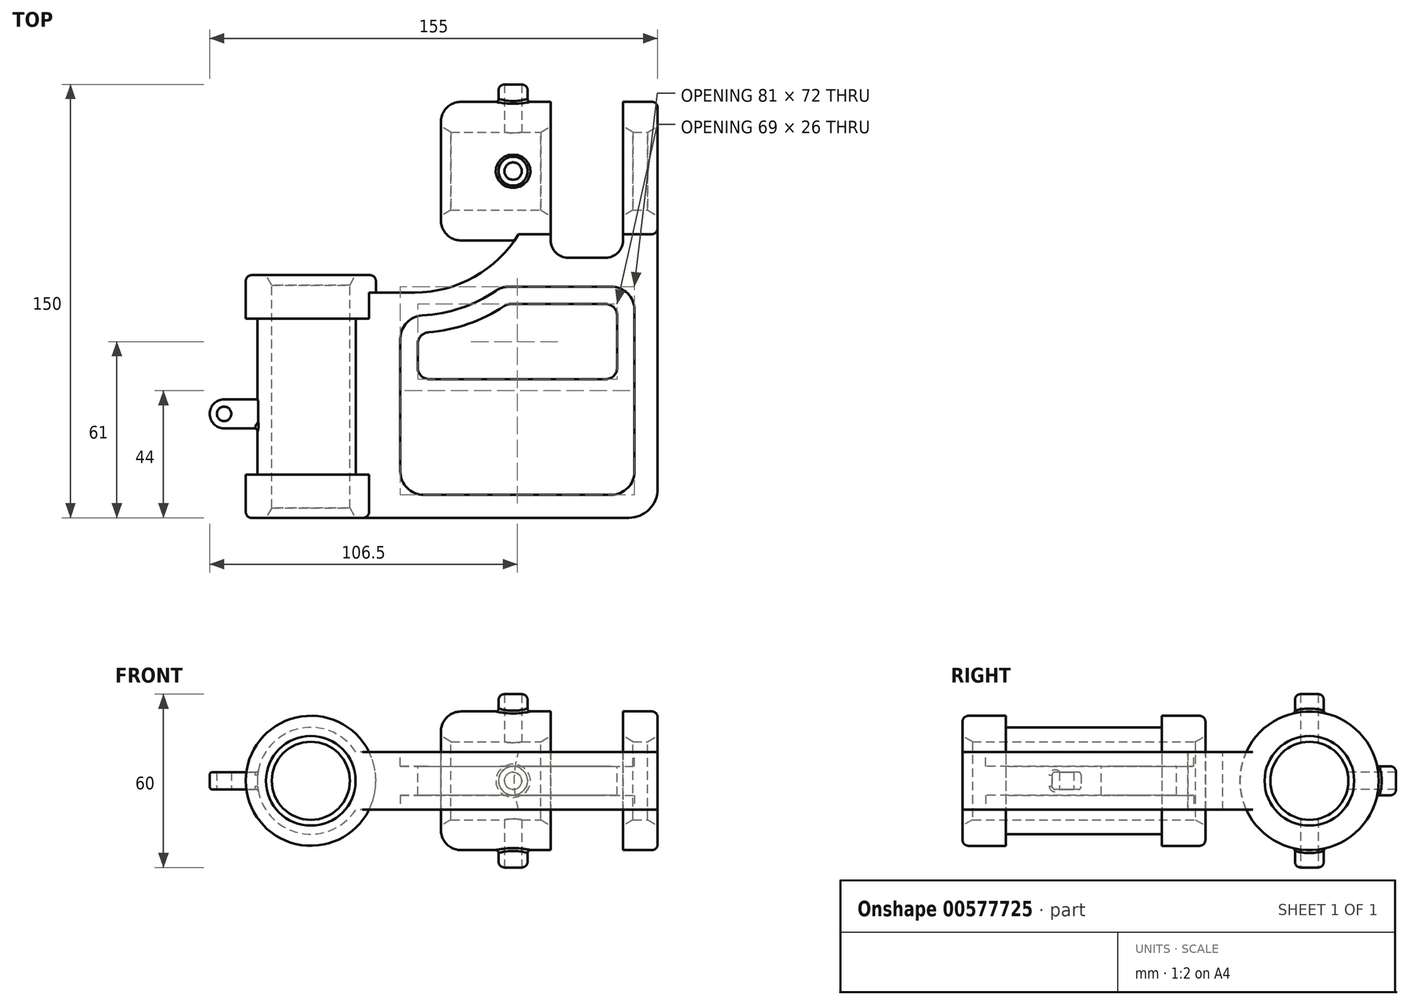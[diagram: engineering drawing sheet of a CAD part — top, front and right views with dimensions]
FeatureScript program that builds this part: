
annotation { "Feature Type Name" : "Feature", "Feature Type Description" : "" }
export const myFeature = defineFeature(function(context is Context, id is Id, definition is map)
    precondition{}
    {
        {
            var Q0;
            Q0=qCreatedBy(makeId("Top.planeOp"),FACE);
            var sketch = newSketch(context, id + "F0", { "sketchPlane" : qUnion([Q0])});
            skLineSegment(sketch, "E0.bottom", {"start": v(-10, 0) * mm, "end": v(-120, 0) * mm});
            skLineSegment(sketch, "E0.top", {"start": v(0, 120) * mm, "end": v(-42, 120) * mm});
            skLineSegment(sketch, "E0.left", {"start": v(0, 10) * mm, "end": v(0, 120) * mm});
            skLineSegment(sketch, "E0.right", {"start": v(-120, 0) * mm, "end": v(-120, 78) * mm});
            skArc(sketch, "E1", {"start": v(-84, 78) * mm, "mid": v(-54.3, 90.3) * mm, "end": v(-42, 120) * mm});
            skLineSegment(sketch, "E2", {"start": v(-84, 78) * mm, "end": v(-120, 78) * mm});
            skPoint(sketch, "E3.visualSharp", {"position": v(0, 0) * mm});
            skArc(sketch, "E3.filletArc", {"start": v(-10, 0) * mm, "mid": v(-2.93, 2.93) * mm, "end": v(0, 10) * mm});
            skSolve(sketch);
        }
        {
            var Q0;
            Q0 = qSketchRegion(id + "F0", true);
            extrude(context, id + "F1", {"entities" : qUnion([Q0]), "endBound" : BoundingType.SYMMETRIC, "depth" : 20 * mm, "offsetDistance" : 25 * mm});
        }
        {
            var Q0;
            Q0=qCreatedBy(makeId("Top.planeOp"),FACE);
            var sketch = newSketch(context, id + "F2", { "sketchPlane" : qUnion([Q0])});
            skLineSegment(sketch, "E4", {"start": v(-75, 120) * mm, "end": v(0, 120) * mm});
            skLineSegment(sketch, "E5", {"start": v(0, 120) * mm, "end": v(0, 142) * mm});
            skLineSegment(sketch, "E6", {"start": v(-2, 144) * mm, "end": v(-68, 144) * mm});
            skLineSegment(sketch, "E7", {"start": v(-75, 137) * mm, "end": v(-75, 120) * mm});
            skLineSegment(sketch, "E8", {"start": v(-75, 120) * mm, "end": v(-98.48, 120) * mm, "construction": true});
            skPoint(sketch, "E9.visualSharp", {"position": v(-75, 144) * mm});
            skArc(sketch, "E9.filletArc", {"start": v(-68, 144) * mm, "mid": v(-72.95, 141.95) * mm, "end": v(-75, 137) * mm});
            skPoint(sketch, "E10.visualSharp", {"position": v(0, 144) * mm});
            skArc(sketch, "E10.filletArc", {"start": v(0, 142) * mm, "mid": v(-0.59, 143.41) * mm, "end": v(-2, 144) * mm});
            skLineSegment(sketch, "E11", {"start": v(-75, 133.5) * mm, "end": v(0, 133.5) * mm, "construction": true});
            skSolve(sketch);
        }
        {
            var Q0;
            Q0=makeQuery(id+"F2.imprint","IMPRINT",FACE,{"disambiguationData":[TD([[makeQuery(id+"F2.imprint","IMPRINT",EDGE,{"derivedFrom":sQuery(id+"F2.wireOp",EDGE,"E4")}),1.0]])]});
            var Q1;
            Q1=sQuery(id+"F2.wireOp",EDGE,"E8");
            revolve(context, id + "F3", {"operationType" : NewBodyOperationType.ADD, "entities" : qUnion([Q0]), "axis" : qUnion([Q1]), "revolveType" : RevolveType.FULL});
        }
        {
            var Q0;
            Q0=qCreatedBy(makeId("Top.planeOp"),FACE);
            var sketch = newSketch(context, id + "F4", { "sketchPlane" : qUnion([Q0])});
            skLineSegment(sketch, "E12", {"start": v(-120, 0) * mm, "end": v(-120, 84) * mm});
            skLineSegment(sketch, "E13", {"start": v(-120, 84) * mm, "end": v(-140.5, 84) * mm});
            skLineSegment(sketch, "E14", {"start": v(-142.5, 82) * mm, "end": v(-142.5, 69) * mm});
            skLineSegment(sketch, "E15", {"start": v(-142.5, 69) * mm, "end": v(-138.5, 69) * mm});
            skLineSegment(sketch, "E16", {"start": v(-138.5, 69) * mm, "end": v(-138.5, 15) * mm});
            skLineSegment(sketch, "E17", {"start": v(-120, 42) * mm, "end": v(-294.47, 42) * mm, "construction": true});
            skLineSegment(sketch, "E18.MirrorCS", {"start": v(-142.5, 15) * mm, "end": v(-138.5, 15) * mm});
            skLineSegment(sketch, "E19.MirrorCS", {"start": v(-142.5, 2) * mm, "end": v(-142.5, 15) * mm});
            skLineSegment(sketch, "E20.MirrorCS", {"start": v(-120, 0) * mm, "end": v(-140.5, 0) * mm});
            skLineSegment(sketch, "E21", {"start": v(-120, 84) * mm, "end": v(-120, 176) * mm, "construction": true});
            skLineSegment(sketch, "E22", {"start": v(-133.5, 84) * mm, "end": v(-133.5, 0) * mm, "construction": true});
            skPoint(sketch, "E23.visualSharp", {"position": v(-142.5, 84) * mm});
            skArc(sketch, "E23.filletArc", {"start": v(-140.5, 84) * mm, "mid": v(-141.91, 83.41) * mm, "end": v(-142.5, 82) * mm});
            skPoint(sketch, "E24.visualSharp", {"position": v(-142.5, 0) * mm});
            skArc(sketch, "E24.filletArc", {"start": v(-142.5, 2) * mm, "mid": v(-141.91, 0.59) * mm, "end": v(-140.5, 0) * mm});
            skSolve(sketch);
        }
        {
            var Q0;
            Q0=makeQuery(id+"F4.imprint","IMPRINT",FACE,{"disambiguationData":[TD([[makeQuery(id+"F4.imprint","IMPRINT",EDGE,{"derivedFrom":sQuery(id+"F4.wireOp",EDGE,"E12")}),1.0]])]});
            var Q1;
            Q1 = qConstructionFilter(qBodyType(qCreatedBy(id + "F4" ,EDGE), BodyType.WIRE), ConstructionObject.NO);
            var Q2;
            Q2=sQuery(id+"F4.wireOp",EDGE,"E21");
            revolve(context, id + "F5", {"operationType" : NewBodyOperationType.ADD, "entities" : qUnion([Q0]), "surfaceEntities" : qUnion([Q1]), "axis" : qUnion([Q2]), "revolveType" : RevolveType.FULL});
        }
        {
            var Q0;
            Q0=qCreatedBy(makeId("Top.planeOp"),FACE);
            var sketch = newSketch(context, id + "F6", { "sketchPlane" : qUnion([Q0])});
            skLineSegment(sketch, "E25", {"start": v(-55, 120) * mm, "end": v(-55, 148) * mm});
            skLineSegment(sketch, "E26", {"start": v(-53, 150) * mm, "end": v(-50, 150) * mm});
            skLineSegment(sketch, "E27", {"start": v(-50, 150) * mm, "end": v(-50, 120) * mm});
            skLineSegment(sketch, "E28", {"start": v(-50, 120) * mm, "end": v(-55, 120) * mm});
            skLineSegment(sketch, "E29", {"start": v(-53, 120) * mm, "end": v(-53, 150) * mm, "construction": true});
            skPoint(sketch, "E30.visualSharp", {"position": v(-55, 150) * mm});
            skArc(sketch, "E30.filletArc", {"start": v(-53, 150) * mm, "mid": v(-54.41, 149.41) * mm, "end": v(-55, 148) * mm});
            skLineSegment(sketch, "E31", {"start": v(-50, 150) * mm, "end": v(-50, 202.5) * mm, "construction": true});
            skSolve(sketch);
        }
        {
            var Q0;
            Q0=makeQuery(id+"F6.imprint","IMPRINT",FACE,{"disambiguationData":[TD([[makeQuery(id+"F6.imprint","IMPRINT",EDGE,{"derivedFrom":sQuery(id+"F6.wireOp",EDGE,"E25")}),-1.0]])]});
            var Q1;
            Q1=sQuery(id+"F6.wireOp",EDGE,"E31");
            revolve(context, id + "F7", {"entities" : qUnion([Q0]), "axis" : qUnion([Q1]), "revolveType" : RevolveType.FULL});
        }
        {
            var Q0;
            Q0=qCreatedBy(makeId("Top.planeOp"),FACE);
            var sketch = newSketch(context, id + "F8", { "sketchPlane" : qUnion([Q0])});
            skLineSegment(sketch, "E32.bottom", {"start": v(-50, 150) * mm, "end": v(-53, 150) * mm});
            skLineSegment(sketch, "E32.top", {"start": v(-50, 120) * mm, "end": v(-53, 120) * mm});
            skLineSegment(sketch, "E32.left", {"start": v(-50, 150) * mm, "end": v(-50, 120) * mm});
            skLineSegment(sketch, "E32.right", {"start": v(-53, 150) * mm, "end": v(-53, 120) * mm});
            skLineSegment(sketch, "E33", {"start": v(-50, 150) * mm, "end": v(-50, 168.1) * mm, "construction": true});
            skSolve(sketch);
        }
        {
            var Q0;
            Q0 = qSketchRegion(id + "F8", true);
            var Q1;
            Q1=sQuery(id+"F8.wireOp",EDGE,"E33");
            revolve(context, id + "F9", {"entities" : qUnion([Q0]), "axis" : qUnion([Q1]), "revolveType" : RevolveType.FULL});
        }
        {
            var Q0;
            Q0=makeQuery(id+"F7.opRevolve","SWEPT_BODY",BODY,{"disambiguationData":[OSD([sQuery(id+"F6.wireOp",EDGE,"E25"),sQuery(id+"F6.wireOp",EDGE,"E26"),sQuery(id+"F6.wireOp",EDGE,"E27"),sQuery(id+"F6.wireOp",EDGE,"E28"),sQuery(id+"F6.wireOp",EDGE,"E30.filletArc")])]});
            var Q1;
            Q1=makeQuery(id+"F9.opRevolve","SWEPT_BODY",BODY,{"disambiguationData":[OSD([sQuery(id+"F8.wireOp",EDGE,"E32.bottom"),sQuery(id+"F8.wireOp",EDGE,"E32.top"),sQuery(id+"F8.wireOp",EDGE,"E32.left"),sQuery(id+"F8.wireOp",EDGE,"E32.right")])]});
            var Q2;
            Q2=sQuery(id+"F2.wireOp",EDGE,"E8");
            circularPattern(context, id + "F10", {"entities" : qUnion([Q0, Q1]), "axis" : qUnion([Q2]), "angle" : 90 * degree, "instanceCount" : 2, "oppositeDirection" : true, "equalSpace" : true});
        }
        {
            var Q0;
            Q0=makeQuery(id+"F7.opRevolve","SWEPT_BODY",BODY,{"disambiguationData":[OSD([sQuery(id+"F6.wireOp",EDGE,"E25"),sQuery(id+"F6.wireOp",EDGE,"E26"),sQuery(id+"F6.wireOp",EDGE,"E27"),sQuery(id+"F6.wireOp",EDGE,"E28"),sQuery(id+"F6.wireOp",EDGE,"E30.filletArc")])]});
            var Q1;
            Q1=makeQuery(id+"F9.opRevolve","SWEPT_BODY",BODY,{"disambiguationData":[OSD([sQuery(id+"F8.wireOp",EDGE,"E32.bottom"),sQuery(id+"F8.wireOp",EDGE,"E32.top"),sQuery(id+"F8.wireOp",EDGE,"E32.left"),sQuery(id+"F8.wireOp",EDGE,"E32.right")])]});
            var Q2;
            Q2=sQuery(id+"F2.wireOp",EDGE,"E8");
            circularPattern(context, id + "F11", {"entities" : qUnion([Q0, Q1]), "axis" : qUnion([Q2]), "angle" : 90 * degree, "instanceCount" : 2, "equalSpace" : true});
        }
        {
            var Q0;
            Q0=makeQuery(id+"F1.opExtrude","SWEPT_BODY",BODY,{"disambiguationData":[OSD([sQuery(id+"F0.wireOp",EDGE,"E0.bottom"),sQuery(id+"F0.wireOp",EDGE,"E0.top"),sQuery(id+"F0.wireOp",EDGE,"E0.left"),sQuery(id+"F0.wireOp",EDGE,"E0.right"),sQuery(id+"F0.wireOp",EDGE,"E1"),sQuery(id+"F0.wireOp",EDGE,"E2"),sQuery(id+"F0.wireOp",EDGE,"E3.filletArc")])]});
            var Q1;
            Q1=makeQuery(id+"F10.opPattern","COPY",BODY,{"derivedFrom":makeQuery(id+"F7.opRevolve","SWEPT_BODY",BODY,{"disambiguationData":[OSD([sQuery(id+"F6.wireOp",EDGE,"E25"),sQuery(id+"F6.wireOp",EDGE,"E26"),sQuery(id+"F6.wireOp",EDGE,"E27"),sQuery(id+"F6.wireOp",EDGE,"E28"),sQuery(id+"F6.wireOp",EDGE,"E30.filletArc")])]}),"instanceName":"1"});
            var Q2;
            Q2=makeQuery(id+"F7.opRevolve","SWEPT_BODY",BODY,{"disambiguationData":[OSD([sQuery(id+"F6.wireOp",EDGE,"E25"),sQuery(id+"F6.wireOp",EDGE,"E26"),sQuery(id+"F6.wireOp",EDGE,"E27"),sQuery(id+"F6.wireOp",EDGE,"E28"),sQuery(id+"F6.wireOp",EDGE,"E30.filletArc")])]});
            var Q3;
            Q3=makeQuery(id+"F11.opPattern","COPY",BODY,{"derivedFrom":makeQuery(id+"F7.opRevolve","SWEPT_BODY",BODY,{"disambiguationData":[OSD([sQuery(id+"F6.wireOp",EDGE,"E25"),sQuery(id+"F6.wireOp",EDGE,"E26"),sQuery(id+"F6.wireOp",EDGE,"E27"),sQuery(id+"F6.wireOp",EDGE,"E28"),sQuery(id+"F6.wireOp",EDGE,"E30.filletArc")])]}),"instanceName":"1"});
            booleanBodies(context, id + "F12", {"operationType" : BooleanOperationType.UNION, "tools" : qUnion([Q0, Q1, Q2, Q3])});
        }
        {
            var Q0;
            Q0=makeQuery(id+"F9.opRevolve","SWEPT_BODY",BODY,{"disambiguationData":[OSD([sQuery(id+"F8.wireOp",EDGE,"E32.bottom"),sQuery(id+"F8.wireOp",EDGE,"E32.top"),sQuery(id+"F8.wireOp",EDGE,"E32.left"),sQuery(id+"F8.wireOp",EDGE,"E32.right")])]});
            var Q1;
            Q1=makeQuery(id+"F10.opPattern","COPY",BODY,{"derivedFrom":makeQuery(id+"F9.opRevolve","SWEPT_BODY",BODY,{"disambiguationData":[OSD([sQuery(id+"F8.wireOp",EDGE,"E32.bottom"),sQuery(id+"F8.wireOp",EDGE,"E32.top"),sQuery(id+"F8.wireOp",EDGE,"E32.left"),sQuery(id+"F8.wireOp",EDGE,"E32.right")])]}),"instanceName":"1"});
            var Q2;
            Q2=makeQuery(id+"F11.opPattern","COPY",BODY,{"derivedFrom":makeQuery(id+"F9.opRevolve","SWEPT_BODY",BODY,{"disambiguationData":[OSD([sQuery(id+"F8.wireOp",EDGE,"E32.bottom"),sQuery(id+"F8.wireOp",EDGE,"E32.top"),sQuery(id+"F8.wireOp",EDGE,"E32.left"),sQuery(id+"F8.wireOp",EDGE,"E32.right")])]}),"instanceName":"1"});
            var Q3;
            Q3=makeQuery(id+"F1.opExtrude","SWEPT_BODY",BODY,{"disambiguationData":[OSD([sQuery(id+"F0.wireOp",EDGE,"E0.bottom"),sQuery(id+"F0.wireOp",EDGE,"E0.top"),sQuery(id+"F0.wireOp",EDGE,"E0.left"),sQuery(id+"F0.wireOp",EDGE,"E0.right"),sQuery(id+"F0.wireOp",EDGE,"E1"),sQuery(id+"F0.wireOp",EDGE,"E2"),sQuery(id+"F0.wireOp",EDGE,"E3.filletArc")])]});
            booleanBodies(context, id + "F13", {"operationType" : BooleanOperationType.SUBTRACTION, "tools" : qUnion([Q0, Q1, Q2]), "targets" : qUnion([Q3])});
        }
        {
            var Q0;
            Q0=qCreatedBy(makeId("Top.planeOp"),FACE);
            var sketch = newSketch(context, id + "F14", { "sketchPlane" : qUnion([Q0])});
            skLineSegment(sketch, "E34", {"start": v(-120, 41) * mm, "end": v(-150, 41) * mm});
            skLineSegment(sketch, "E35", {"start": v(-150, 41) * mm, "end": v(-150, 31) * mm, "construction": true});
            skLineSegment(sketch, "E36", {"start": v(-150, 31) * mm, "end": v(-120, 31) * mm});
            skLineSegment(sketch, "E37", {"start": v(-120, 31) * mm, "end": v(-120, 41) * mm});
            skArc(sketch, "E38", {"start": v(-150, 41) * mm, "mid": v(-155, 36) * mm, "end": v(-150, 31) * mm});
            skCircle(sketch, "E39", {"center": v(-150, 36) * mm, "radius": 2.5 * mm});
            skSolve(sketch);
        }
        {
            var Q0;
            Q0=makeQuery(id+"F14.imprint","IMPRINT",FACE,{"disambiguationData":[TD([[makeQuery(id+"F14.imprint","IMPRINT",EDGE,{"derivedFrom":sQuery(id+"F14.wireOp",EDGE,"E34")}),1.0]])]});
            extrude(context, id + "F15", {"entities" : qUnion([Q0]), "operationType" : NewBodyOperationType.ADD, "endBound" : BoundingType.SYMMETRIC, "depth" : 6 * mm, "offsetDistance" : 25 * mm});
        }
        {
            var Q0;
            Q0=makeQuery(id+"F15.opExtrude","CAP_EDGE",EDGE,{"disambiguationData":[OSD([sQuery(id+"F14.wireOp",EDGE,"E36")])],"isStart":false});
            var Q1;
            Q1=makeQuery(id+"F15.opExtrude","CAP_EDGE",EDGE,{"disambiguationData":[OSD([sQuery(id+"F14.wireOp",EDGE,"E36")])],"isStart":true});
            var Q2;
            Q2=makeQuery(id+"F15.boolean.opBoolean","INTERSECT",EDGE,{"derivedFrom":[makeQuery(id+"F5.opRevolve","SWEPT_FACE",FACE,{"disambiguationData":[OSD([sQuery(id+"F4.wireOp",EDGE,"E16")])]}),makeQuery(id+"F15.opExtrude","SWEPT_FACE",FACE,{"disambiguationData":[OSD([sQuery(id+"F14.wireOp",EDGE,"E36")])]})]});
            fillet(context, id + "F16", {"entities" : qUnion([Q0, Q1, Q2]), "radius" : 1 * mm, "tangentPropagation" : true, "allowEdgeOverflow" : false});
        }
        {
            var Q0;
            Q0=makeQuery(id+"F12.opBoolean","INTERSECT",EDGE,{"disambiguationData":[OD(0.0)],"derivedFrom":[makeQuery(id+"F3.opRevolve","SWEPT_FACE",FACE,{"disambiguationData":[OSD([sQuery(id+"F2.wireOp",EDGE,"E6")])]}),makeQuery(id+"F11.opPattern","COPY",FACE,{"derivedFrom":makeQuery(id+"F7.opRevolve","SWEPT_FACE",FACE,{"disambiguationData":[OSD([sQuery(id+"F6.wireOp",EDGE,"E25")])]}),"instanceName":"1"})]});
            var Q1;
            Q1=makeQuery(id+"F12.opBoolean","INTERSECT",EDGE,{"derivedFrom":[makeQuery(id+"F3.opRevolve","SWEPT_FACE",FACE,{"disambiguationData":[OSD([sQuery(id+"F2.wireOp",EDGE,"E6")])]}),makeQuery(id+"F7.opRevolve","SWEPT_FACE",FACE,{"disambiguationData":[OSD([sQuery(id+"F6.wireOp",EDGE,"E25")])]})]});
            var Q2;
            Q2=makeQuery(id+"F12.opBoolean","INTERSECT",EDGE,{"disambiguationData":[OD(1.0)],"derivedFrom":[makeQuery(id+"F3.opRevolve","SWEPT_FACE",FACE,{"disambiguationData":[OSD([sQuery(id+"F2.wireOp",EDGE,"E6")])]}),makeQuery(id+"F11.opPattern","COPY",FACE,{"derivedFrom":makeQuery(id+"F7.opRevolve","SWEPT_FACE",FACE,{"disambiguationData":[OSD([sQuery(id+"F6.wireOp",EDGE,"E25")])]}),"instanceName":"1"})]});
            fillet(context, id + "F17", {"entities" : qUnion([Q0, Q1, Q2]), "radius" : 1 * mm, "tangentPropagation" : true, "allowEdgeOverflow" : false});
        }
        {
            var Q0;
            Q0=qCreatedBy(makeId("Top.planeOp"),FACE);
            var sketch = newSketch(context, id + "F18", { "sketchPlane" : qUnion([Q0])});
            skLineSegment(sketch, "E40.bottom", {"start": v(-37, 144) * mm, "end": v(-12, 144) * mm});
            skLineSegment(sketch, "E40.top", {"start": v(-31, 90) * mm, "end": v(-18, 90) * mm});
            skLineSegment(sketch, "E40.left", {"start": v(-37, 144) * mm, "end": v(-37, 96) * mm});
            skLineSegment(sketch, "E40.right", {"start": v(-12, 144) * mm, "end": v(-12, 96) * mm});
            skPoint(sketch, "E41.visualSharp", {"position": v(-37, 90) * mm});
            skArc(sketch, "E41.filletArc", {"start": v(-37, 96) * mm, "mid": v(-35.24, 91.76) * mm, "end": v(-31, 90) * mm});
            skPoint(sketch, "E42.visualSharp", {"position": v(-12, 90) * mm});
            skArc(sketch, "E42.filletArc", {"start": v(-18, 90) * mm, "mid": v(-13.76, 91.76) * mm, "end": v(-12, 96) * mm});
            skSolve(sketch);
        }
        {
            var Q0;
            Q0 = qSketchRegion(id + "F18", true);
            extrude(context, id + "F19", {"entities" : qUnion([Q0]), "operationType" : NewBodyOperationType.REMOVE, "endBound" : BoundingType.SYMMETRIC, "oppositeDirection" : true, "depth" : 100 * mm, "offsetDistance" : 25 * mm});
        }
        {
            var Q0;
            Q0=qCreatedBy(makeId("Top.planeOp"),FACE);
            var sketch = newSketch(context, id + "F20", { "sketchPlane" : qUnion([Q0])});
            skLineSegment(sketch, "E43", {"start": v(-120, 0) * mm, "end": v(-120, 84) * mm});
            skLineSegment(sketch, "E44", {"start": v(-120, 84) * mm, "end": v(-135.5, 84) * mm});
            skLineSegment(sketch, "E45", {"start": v(-135.5, 84) * mm, "end": v(-133.5, 80.54) * mm});
            skLineSegment(sketch, "E46", {"start": v(-133.5, 80.54) * mm, "end": v(-133.5, 3.46) * mm});
            skLineSegment(sketch, "E47", {"start": v(-120, 42) * mm, "end": v(-142.84, 42) * mm, "construction": true});
            skPoint(sketch, "E47.endSnap0", {"position": v(-120, 42) * mm});
            skLineSegment(sketch, "E48.MirrorCS", {"start": v(-135.5, 0) * mm, "end": v(-133.5, 3.46) * mm});
            skLineSegment(sketch, "E49.MirrorCS", {"start": v(-120, 0) * mm, "end": v(-135.5, 0) * mm});
            skLineSegment(sketch, "E50", {"start": v(-120, 84) * mm, "end": v(-120, 94.84) * mm, "construction": true});
            skSolve(sketch);
        }
        {
            var Q0;
            Q0=makeQuery(id+"F20.imprint","IMPRINT",FACE,{"disambiguationData":[TD([[makeQuery(id+"F20.imprint","IMPRINT",EDGE,{"derivedFrom":sQuery(id+"F20.wireOp",EDGE,"E43")}),1.0]])]});
            var Q1;
            Q1=sQuery(id+"F20.wireOp",EDGE,"E50");
            revolve(context, id + "F21", {"operationType" : NewBodyOperationType.REMOVE, "entities" : qUnion([Q0]), "axis" : qUnion([Q1]), "revolveType" : RevolveType.FULL, "oppositeDirection" : true});
        }
        {
            var Q0;
            Q0=qCreatedBy(makeId("Top.planeOp"),FACE);
            var sketch = newSketch(context, id + "F22", { "sketchPlane" : qUnion([Q0])});
            skLineSegment(sketch, "E51", {"start": v(-75, 120) * mm, "end": v(-37, 120) * mm});
            skLineSegment(sketch, "E52", {"start": v(-37, 120) * mm, "end": v(-37, 135.5) * mm});
            skLineSegment(sketch, "E53", {"start": v(-37, 135.5) * mm, "end": v(-40.46, 133.5) * mm});
            skLineSegment(sketch, "E54", {"start": v(-40.46, 133.5) * mm, "end": v(-71.54, 133.5) * mm});
            skLineSegment(sketch, "E55", {"start": v(-56, 120) * mm, "end": v(-56, 187.01) * mm, "construction": true});
            skLineSegment(sketch, "E56.MirrorCS", {"start": v(-75, 135.5) * mm, "end": v(-71.54, 133.5) * mm});
            skLineSegment(sketch, "E57.MirrorCS", {"start": v(-75, 120) * mm, "end": v(-75, 135.5) * mm});
            skLineSegment(sketch, "E58", {"start": v(-12, 120) * mm, "end": v(0, 120) * mm});
            skLineSegment(sketch, "E59", {"start": v(0, 120) * mm, "end": v(0, 135.5) * mm});
            skLineSegment(sketch, "E60", {"start": v(0, 135.5) * mm, "end": v(-3.46, 133.5) * mm});
            skLineSegment(sketch, "E61", {"start": v(-3.46, 133.5) * mm, "end": v(-8.54, 133.5) * mm});
            skLineSegment(sketch, "E62", {"start": v(-6, 120) * mm, "end": v(-6, 150.05) * mm, "construction": true});
            skLineSegment(sketch, "E63.MirrorCS", {"start": v(-12, 135.5) * mm, "end": v(-8.54, 133.5) * mm});
            skLineSegment(sketch, "E64.MirrorCS", {"start": v(-12, 120) * mm, "end": v(-12, 135.5) * mm});
            skLineSegment(sketch, "E65", {"start": v(-37, 135.5) * mm, "end": v(-12, 135.5) * mm, "construction": true});
            skLineSegment(sketch, "E66", {"start": v(0, 120) * mm, "end": v(35.99, 120) * mm, "construction": true});
            skSolve(sketch);
        }
        {
            var Q0;
            Q0 = qSketchRegion(id + "F22", true);
            var Q1;
            Q1=sQuery(id+"F22.wireOp",EDGE,"E66");
            revolve(context, id + "F23", {"operationType" : NewBodyOperationType.REMOVE, "entities" : qUnion([Q0]), "axis" : qUnion([Q1]), "revolveType" : RevolveType.FULL, "oppositeDirection" : true});
        }
        {
            var Q0;
            Q0=makeQuery(id+"F1.opExtrude","CAP_FACE",FACE,{"disambiguationData":[OSD([sQuery(id+"F0.wireOp",EDGE,"E0.bottom"),sQuery(id+"F0.wireOp",EDGE,"E0.top"),sQuery(id+"F0.wireOp",EDGE,"E0.left"),sQuery(id+"F0.wireOp",EDGE,"E0.right"),sQuery(id+"F0.wireOp",EDGE,"E1"),sQuery(id+"F0.wireOp",EDGE,"E2"),sQuery(id+"F0.wireOp",EDGE,"E3.filletArc")])],"isStart":false});
            var sketch = newSketch(context, id + "F24", { "sketchPlane" : qUnion([Q0])});
            skLineSegment(sketch, "E67", {"start": v(-81, 8) * mm, "end": v(-16, 8) * mm});
            skLineSegment(sketch, "E68", {"start": v(-8, 16) * mm, "end": v(-8, 72) * mm});
            skLineSegment(sketch, "E69", {"start": v(-16, 80) * mm, "end": v(-51.44, 80) * mm});
            skLineSegment(sketch, "E70", {"start": v(-89, 62.08) * mm, "end": v(-89, 16) * mm});
            skArc(sketch, "E71", {"start": v(-81.41, 70.07) * mm, "mid": v(-68.09, 72.6) * mm, "end": v(-55.93, 78.62) * mm});
            skPoint(sketch, "E72.visualSharp", {"position": v(-8, 8) * mm});
            skArc(sketch, "E72.filletArc", {"start": v(-16, 8) * mm, "mid": v(-10.34, 10.34) * mm, "end": v(-8, 16) * mm});
            skPoint(sketch, "E73.visualSharp", {"position": v(-8, 80) * mm});
            skArc(sketch, "E73.filletArc", {"start": v(-8, 72) * mm, "mid": v(-10.34, 77.66) * mm, "end": v(-16, 80) * mm});
            skPoint(sketch, "E74.visualSharp", {"position": v(-89, 8) * mm});
            skArc(sketch, "E74.filletArc", {"start": v(-89, 16) * mm, "mid": v(-86.66, 10.34) * mm, "end": v(-81, 8) * mm});
            skPoint(sketch, "E75.visualSharp", {"position": v(-89, 70.25) * mm});
            skArc(sketch, "E75.filletArc", {"start": v(-81.41, 70.07) * mm, "mid": v(-86.8, 67.59) * mm, "end": v(-89, 62.08) * mm});
            skPoint(sketch, "E76.visualSharp", {"position": v(-54, 80) * mm});
            skArc(sketch, "E76.filletArc", {"start": v(-51.44, 80) * mm, "mid": v(-53.8, 79.65) * mm, "end": v(-55.93, 78.62) * mm});
            skSolve(sketch);
        }
        {
            var Q0;
            Q0 = qSketchRegion(id + "F24", true);
            extrude(context, id + "F25", {"entities" : qUnion([Q0]), "oppositeDirection" : true, "depth" : 5 * mm, "offsetDistance" : 25 * mm});
        }
        {
            var Q0;
            Q0=makeQuery(id+"F25.opExtrude","SWEPT_BODY",BODY,{"disambiguationData":[OSD([sQuery(id+"F24.wireOp",EDGE,"E67"),sQuery(id+"F24.wireOp",EDGE,"E68"),sQuery(id+"F24.wireOp",EDGE,"E69"),sQuery(id+"F24.wireOp",EDGE,"E70"),sQuery(id+"F24.wireOp",EDGE,"E71"),sQuery(id+"F24.wireOp",EDGE,"E72.filletArc"),sQuery(id+"F24.wireOp",EDGE,"E73.filletArc"),sQuery(id+"F24.wireOp",EDGE,"E74.filletArc"),sQuery(id+"F24.wireOp",EDGE,"E75.filletArc"),sQuery(id+"F24.wireOp",EDGE,"E76.filletArc")])]});
            var Q1;
            Q1=qCreatedBy(makeId("Top.planeOp"),FACE);
            mirror(context, id + "F26", {"entities" : qUnion([Q0]), "mirrorPlane" : qUnion([Q1])});
        }
        {
            var Q0;
            Q0=makeQuery(id+"F25.opExtrude","SWEPT_BODY",BODY,{"disambiguationData":[OSD([sQuery(id+"F24.wireOp",EDGE,"E67"),sQuery(id+"F24.wireOp",EDGE,"E68"),sQuery(id+"F24.wireOp",EDGE,"E69"),sQuery(id+"F24.wireOp",EDGE,"E70"),sQuery(id+"F24.wireOp",EDGE,"E71"),sQuery(id+"F24.wireOp",EDGE,"E72.filletArc"),sQuery(id+"F24.wireOp",EDGE,"E73.filletArc"),sQuery(id+"F24.wireOp",EDGE,"E74.filletArc"),sQuery(id+"F24.wireOp",EDGE,"E75.filletArc"),sQuery(id+"F24.wireOp",EDGE,"E76.filletArc")])]});
            var Q1;
            Q1=makeQuery(id+"F26.opPattern","COPY",BODY,{"derivedFrom":makeQuery(id+"F25.opExtrude","SWEPT_BODY",BODY,{"disambiguationData":[OSD([sQuery(id+"F24.wireOp",EDGE,"E67"),sQuery(id+"F24.wireOp",EDGE,"E68"),sQuery(id+"F24.wireOp",EDGE,"E69"),sQuery(id+"F24.wireOp",EDGE,"E70"),sQuery(id+"F24.wireOp",EDGE,"E71"),sQuery(id+"F24.wireOp",EDGE,"E72.filletArc"),sQuery(id+"F24.wireOp",EDGE,"E73.filletArc"),sQuery(id+"F24.wireOp",EDGE,"E74.filletArc"),sQuery(id+"F24.wireOp",EDGE,"E75.filletArc"),sQuery(id+"F24.wireOp",EDGE,"E76.filletArc")])]}),"instanceName":"1"});
            var Q2;
            Q2=makeQuery(id+"F1.opExtrude","SWEPT_BODY",BODY,{"disambiguationData":[OSD([sQuery(id+"F0.wireOp",EDGE,"E0.bottom"),sQuery(id+"F0.wireOp",EDGE,"E0.top"),sQuery(id+"F0.wireOp",EDGE,"E0.left"),sQuery(id+"F0.wireOp",EDGE,"E0.right"),sQuery(id+"F0.wireOp",EDGE,"E1"),sQuery(id+"F0.wireOp",EDGE,"E2"),sQuery(id+"F0.wireOp",EDGE,"E3.filletArc")])]});
            booleanBodies(context, id + "F27", {"operationType" : BooleanOperationType.SUBTRACTION, "tools" : qUnion([Q0, Q1]), "targets" : qUnion([Q2])});
        }
        {
            var Q0;
            Q0=qCreatedBy(makeId("Top.planeOp"),FACE);
            var sketch = newSketch(context, id + "F28", { "sketchPlane" : qUnion([Q0])});
            skLineSegment(sketch, "E77", {"start": v(-83, 60.2) * mm, "end": v(-83, 52) * mm});
            skLineSegment(sketch, "E78", {"start": v(-79, 48) * mm, "end": v(-18, 48) * mm});
            skLineSegment(sketch, "E79", {"start": v(-14, 52) * mm, "end": v(-14, 70) * mm});
            skLineSegment(sketch, "E80", {"start": v(-18, 74) * mm, "end": v(-50.83, 74) * mm});
            skArc(sketch, "E81", {"start": v(-79.33, 64.2) * mm, "mid": v(-65.61, 67.1) * mm, "end": v(-53.04, 73.33) * mm});
            skPoint(sketch, "E82.visualSharp", {"position": v(-52.06, 74) * mm});
            skArc(sketch, "E82.filletArc", {"start": v(-50.83, 74) * mm, "mid": v(-51.99, 73.83) * mm, "end": v(-53.04, 73.33) * mm});
            skPoint(sketch, "E83.visualSharp", {"position": v(-14, 74) * mm});
            skArc(sketch, "E83.filletArc", {"start": v(-14, 70) * mm, "mid": v(-15.17, 72.83) * mm, "end": v(-18, 74) * mm});
            skPoint(sketch, "E84.visualSharp", {"position": v(-14, 48) * mm});
            skArc(sketch, "E84.filletArc", {"start": v(-18, 48) * mm, "mid": v(-15.17, 49.17) * mm, "end": v(-14, 52) * mm});
            skPoint(sketch, "E85.visualSharp", {"position": v(-83, 48) * mm});
            skArc(sketch, "E85.filletArc", {"start": v(-83, 52) * mm, "mid": v(-81.83, 49.17) * mm, "end": v(-79, 48) * mm});
            skPoint(sketch, "E86.visualSharp", {"position": v(-83, 64) * mm});
            skArc(sketch, "E86.filletArc", {"start": v(-79.33, 64.2) * mm, "mid": v(-81.94, 62.92) * mm, "end": v(-83, 60.2) * mm});
            skSolve(sketch);
        }
        {
            var Q0;
            Q0 = qSketchRegion(id + "F28", true);
            extrude(context, id + "F29", {"entities" : qUnion([Q0]), "operationType" : NewBodyOperationType.REMOVE, "endBound" : BoundingType.SYMMETRIC, "oppositeDirection" : true, "depth" : 100 * mm, "offsetDistance" : 25 * mm});
        }
    });
